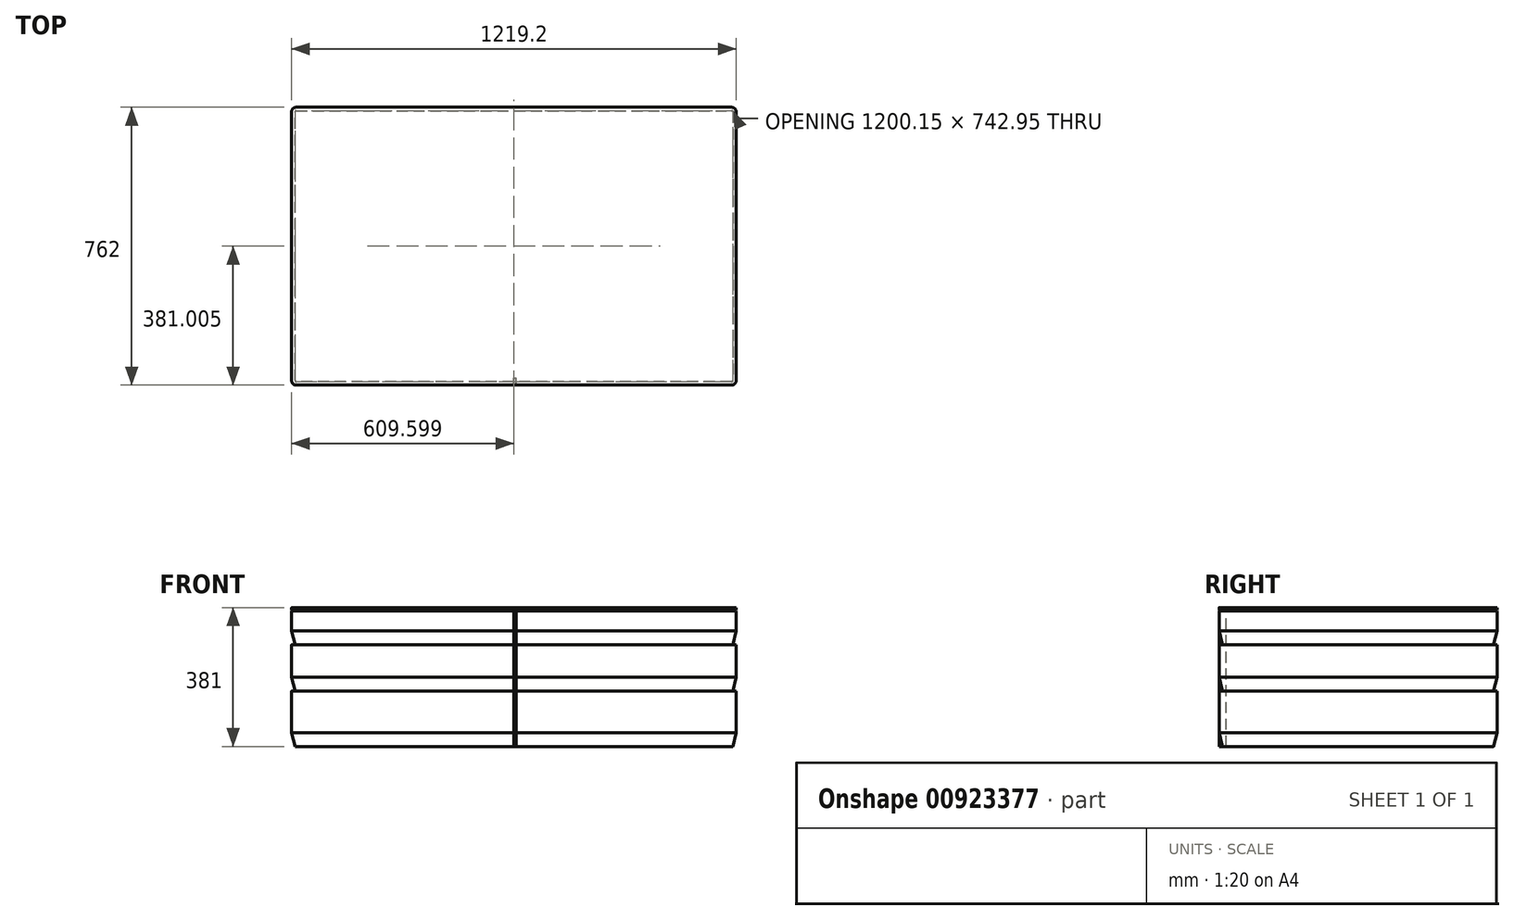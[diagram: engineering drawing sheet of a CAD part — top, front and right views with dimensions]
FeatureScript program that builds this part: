
annotation { "Feature Type Name" : "Feature", "Feature Type Description" : "" }
export const myFeature = defineFeature(function(context is Context, id is Id, definition is map)
    precondition{}
    {
        {
            var Q0;
            Q0=qCreatedBy(makeId("Top.planeOp"),FACE);
            var sketch = newSketch(context, id + "F0", { "sketchPlane" : qUnion([Q0])});
            skLineSegment(sketch, "E0.bottom", {"start": v(-1153.85, 736.91) * mm, "end": v(39.95, 736.91) * mm});
            skLineSegment(sketch, "E0.top", {"start": v(-1153.85, -25.09) * mm, "end": v(39.95, -25.09) * mm});
            skLineSegment(sketch, "E0.left", {"start": v(-1166.55, 724.21) * mm, "end": v(-1166.55, -12.39) * mm});
            skLineSegment(sketch, "E0.right", {"start": v(52.65, 724.21) * mm, "end": v(52.65, -12.39) * mm});
            skPoint(sketch, "E1.visualSharp", {"position": v(-1166.55, 736.91) * mm});
            skArc(sketch, "E1.filletArc", {"start": v(-1153.85, 736.91) * mm, "mid": v(-1162.83, 733.2) * mm, "end": v(-1166.55, 724.21) * mm});
            skPoint(sketch, "E2.visualSharp", {"position": v(-1166.55, -25.09) * mm});
            skArc(sketch, "E2.filletArc", {"start": v(-1166.55, -12.39) * mm, "mid": v(-1162.83, -21.37) * mm, "end": v(-1153.85, -25.09) * mm});
            skPoint(sketch, "E3.visualSharp", {"position": v(52.65, -25.09) * mm});
            skArc(sketch, "E3.filletArc", {"start": v(39.95, -25.09) * mm, "mid": v(48.93, -21.37) * mm, "end": v(52.65, -12.39) * mm});
            skPoint(sketch, "E4.visualSharp", {"position": v(52.65, 736.91) * mm});
            skArc(sketch, "E4.filletArc", {"start": v(52.65, 724.21) * mm, "mid": v(48.93, 733.2) * mm, "end": v(39.95, 736.91) * mm});
            skPoint(sketch, "E5", {"position": v(-556.95, -25.09) * mm});
            skLineSegment(sketch, "E6.bottom", {"start": v(-560.13, -25.09) * mm, "end": v(-553.78, -25.09) * mm});
            skLineSegment(sketch, "E7.left", {"start": v(-560.13, -25.09) * mm, "end": v(-560.13, -25.09) * mm});
            skLineSegment(sketch, "E7.right", {"start": v(-553.78, -25.09) * mm, "end": v(-553.78, -25.09) * mm});
            skLineSegment(sketch, "E8.top", {"start": v(-1166.55, 38.41) * mm, "end": v(-1103.05, 38.41) * mm});
            skLineSegment(sketch, "E8.right", {"start": v(-1103.05, -25.09) * mm, "end": v(-1103.05, 38.41) * mm});
            skLineSegment(sketch, "E9.bottom", {"start": v(-1166.55, 38.41) * mm, "end": v(-1147.5, 38.41) * mm});
            skLineSegment(sketch, "E9.left", {"start": v(-1166.55, 38.41) * mm, "end": v(-1166.55, 40) * mm});
            skLineSegment(sketch, "E10.bottom", {"start": v(-1103.05, -25.09) * mm, "end": v(-1101.46, -25.09) * mm});
            skLineSegment(sketch, "E10.left", {"start": v(-1103.05, -25.09) * mm, "end": v(-1103.05, -6.04) * mm});
            skSolve(sketch);
        }
        {
            var Q0;
            Q0=makeQuery(id+"F0.imprint","IMPRINT",FACE,{"disambiguationData":[TD([[makeQuery(id+"F0.imprint","IMPRINT",EDGE,{"derivedFrom":sQuery(id+"F0.wireOp",EDGE,"E0.bottom")}),-1.0]])]});
            var Q1;
            Q1=makeQuery(id+"F0.imprint","IMPRINT",FACE,{"disambiguationData":[TD([[makeQuery(id+"F0.imprint","IMPRINT",EDGE,{"derivedFrom":sQuery(id+"F0.wireOp",EDGE,"02rgMuwA-EyWu-0coL-EE2w-9yArAnqPD3th.bottom")}),-1.0]])]});
            var Q2;
            {var subQ0=sQuery(id+"F0.wireOp",EDGE,"JKqXYhlD-zWEc-dG3e-kvRR-2U4jhGjXMaC9.left");Q2=makeQuery(id+"F0.imprint","IMPRINT",FACE,{"disambiguationData":[TD([[makeQuery(id+"F0.imprint","IMPRINT",EDGE,{"derivedFrom":subQ0}),1.0]])]});}
            var Q3;
            {var subQ0=sQuery(id+"F0.wireOp",EDGE,"JKqXYhlD-zWEc-dG3e-kvRR-2U4jhGjXMaC9.bottom");Q3=makeQuery(id+"F0.imprint","IMPRINT",FACE,{"disambiguationData":[TD([[makeQuery(id+"F0.imprint","IMPRINT",EDGE,{"derivedFrom":subQ0}),1.0]])]});}
            var Q4;
            {var subQ0=sQuery(id+"F0.wireOp",EDGE,"JKqXYhlD-zWEc-dG3e-kvRR-2U4jhGjXMaC9.top");Q4=makeQuery(id+"F0.imprint","IMPRINT",FACE,{"disambiguationData":[TD([[makeQuery(id+"F0.imprint","IMPRINT",EDGE,{"derivedFrom":subQ0}),-1.0]])]});}
            var Q5;
            {var subQ0=sQuery(id+"F0.wireOp",EDGE,"JKqXYhlD-zWEc-dG3e-kvRR-2U4jhGjXMaC9.bottom");Q5=makeQuery(id+"F0.imprint","IMPRINT",FACE,{"disambiguationData":[TD([[makeQuery(id+"F0.imprint","IMPRINT",EDGE,{"derivedFrom":subQ0}),-1.0]])]});}
            var Q6;
            {var subQ0=sQuery(id+"F0.wireOp",EDGE,"JKqXYhlD-zWEc-dG3e-kvRR-2U4jhGjXMaC9.top");Q6=makeQuery(id+"F0.imprint","IMPRINT",FACE,{"disambiguationData":[TD([[makeQuery(id+"F0.imprint","IMPRINT",EDGE,{"derivedFrom":subQ0}),1.0]])]});}
            var Q7;
            {var subQ0=sQuery(id+"F0.wireOp",EDGE,"4L7YUCBR-3QsD-YcSa-PjCd-UrCzx3tGgLWM");Q7=makeQuery(id+"F0.imprint","IMPRINT",FACE,{"disambiguationData":[TD([[makeQuery(id+"F0.imprint","IMPRINT",EDGE,{"derivedFrom":subQ0}),1.0]])]});}
            var Q8;
            {var subQ0=sQuery(id+"F0.wireOp",EDGE,"B6Vmpnqa-0J3w-GW8c-4OqU-9oorpA2SGJfZ");Q8=makeQuery(id+"F0.imprint","IMPRINT",FACE,{"disambiguationData":[TD([[makeQuery(id+"F0.imprint","IMPRINT",EDGE,{"derivedFrom":subQ0}),-1.0]])]});}
            var Q9;
            Q9=makeQuery(id+"F0.imprint","IMPRINT",FACE,{"disambiguationData":[TD([[makeQuery(id+"F0.imprint","IMPRINT",EDGE,{"derivedFrom":sQuery(id+"F0.wireOp",EDGE,"E6.top")}),-1.0]])]});
            var Q10;
            {var subQ0=sQuery(id+"F0.wireOp",EDGE,"E2.filletArc");Q10=makeQuery(id+"F0.imprint","IMPRINT",FACE,{"disambiguationData":[TD([[makeQuery(id+"F0.imprint","IMPRINT",EDGE,{"derivedFrom":subQ0}),1.0]])]});}
            var Q11;
            Q11=makeQuery(id+"F0.imprint","IMPRINT",FACE,{"disambiguationData":[TD([[makeQuery(id+"F0.imprint","IMPRINT",EDGE,{"derivedFrom":sQuery(id+"F0.wireOp",EDGE,"E9.bottom")}),1.0]])]});
            var Q12;
            Q12=makeQuery(id+"F0.imprint","IMPRINT",FACE,{"disambiguationData":[TD([[makeQuery(id+"F0.imprint","IMPRINT",EDGE,{"derivedFrom":sQuery(id+"F0.wireOp",EDGE,"E10.bottom")}),1.0]])]});
            extrude(context, id + "F1", {"entities" : qUnion([Q0, Q1, Q2, Q3, Q4, Q5, Q6, Q7, Q8, Q9, Q10, Q11, Q12]), "oppositeDirection" : true, "depth" : 6.35 * mm, "offsetDistance" : 25.4 * mm});
        }
        {
            var Q0;
            Q0=makeQuery(id+"F0.imprint","IMPRINT",FACE,{"disambiguationData":[TD([[makeQuery(id+"F0.imprint","IMPRINT",EDGE,{"derivedFrom":sQuery(id+"F0.wireOp",EDGE,"E0.bottom")}),-1.0]])]});
            var Q1;
            Q1=makeQuery(id+"F0.imprint","IMPRINT",FACE,{"disambiguationData":[TD([[makeQuery(id+"F0.imprint","IMPRINT",EDGE,{"derivedFrom":sQuery(id+"F0.wireOp",EDGE,"02rgMuwA-EyWu-0coL-EE2w-9yArAnqPD3th.bottom")}),-1.0]])]});
            var Q2;
            Q2=makeQuery(id+"F0.imprint","IMPRINT",FACE,{"disambiguationData":[TD([[makeQuery(id+"F0.imprint","IMPRINT",EDGE,{"derivedFrom":sQuery(id+"F0.wireOp",EDGE,"JKqXYhlD-zWEc-dG3e-kvRR-2U4jhGjXMaC9.bottom")}),-1.0]])]});
            var Q3;
            {var subQ0=sQuery(id+"F0.wireOp",EDGE,"E2.filletArc");Q3=makeQuery(id+"F0.imprint","IMPRINT",FACE,{"disambiguationData":[TD([[makeQuery(id+"F0.imprint","IMPRINT",EDGE,{"derivedFrom":subQ0}),1.0]])]});}
            extrude(context, id + "F2", {"entities" : qUnion([Q0, Q1, Q2, Q3]), "oppositeDirection" : true, "depth" : 101.6 * mm, "offsetDistance" : 25.4 * mm, "hasSecondDirection" : true, "secondDirectionOppositeDirection" : true, "secondDirectionDepth" : 9.52 * mm});
        }
        {
            var Q0;
            Q0=makeQuery(id+"F2.opExtrude","CAP_FACE",FACE,{"disambiguationData":[OSD([sQuery(id+"F0.wireOp",EDGE,"E0.bottom"),sQuery(id+"F0.wireOp",EDGE,"E0.top"),sQuery(id+"F0.wireOp",EDGE,"E0.left"),sQuery(id+"F0.wireOp",EDGE,"E0.right"),sQuery(id+"F0.wireOp",EDGE,"E1.filletArc"),sQuery(id+"F0.wireOp",EDGE,"E2.filletArc"),sQuery(id+"F0.wireOp",EDGE,"E3.filletArc"),sQuery(id+"F0.wireOp",EDGE,"E4.filletArc")])],"isStart":false});
            chamfer(context, id + "F3", {"entities" : qUnion([Q0]), "chamferType" : ChamferType.TWO_OFFSETS, "width1" : 38.1 * mm, "oppositeDirection" : true, "width2" : 9.52 * mm, "tangentPropagation" : true});
        }
        {
            var Q0;
            Q0=makeQuery(id+"F0.imprint","IMPRINT",FACE,{"disambiguationData":[TD([[makeQuery(id+"F0.imprint","IMPRINT",EDGE,{"derivedFrom":sQuery(id+"F0.wireOp",EDGE,"E0.bottom")}),-1.0]])]});
            var Q1;
            Q1=makeQuery(id+"F0.imprint","IMPRINT",FACE,{"disambiguationData":[TD([[makeQuery(id+"F0.imprint","IMPRINT",EDGE,{"derivedFrom":sQuery(id+"F0.wireOp",EDGE,"JKqXYhlD-zWEc-dG3e-kvRR-2U4jhGjXMaC9.bottom")}),-1.0]])]});
            var Q2;
            Q2=makeQuery(id+"F0.imprint","IMPRINT",FACE,{"disambiguationData":[TD([[makeQuery(id+"F0.imprint","IMPRINT",EDGE,{"derivedFrom":sQuery(id+"F0.wireOp",EDGE,"02rgMuwA-EyWu-0coL-EE2w-9yArAnqPD3th.bottom")}),-1.0]])]});
            var Q3;
            {var subQ0=sQuery(id+"F0.wireOp",EDGE,"E2.filletArc");Q3=makeQuery(id+"F0.imprint","IMPRINT",FACE,{"disambiguationData":[TD([[makeQuery(id+"F0.imprint","IMPRINT",EDGE,{"derivedFrom":subQ0}),1.0]])]});}
            extrude(context, id + "F4", {"entities" : qUnion([Q0, Q1, Q2, Q3]), "operationType" : NewBodyOperationType.ADD, "oppositeDirection" : true, "depth" : 228.6 * mm, "offsetDistance" : 25.4 * mm, "hasSecondDirection" : true, "secondDirectionOppositeDirection" : true, "secondDirectionDepth" : 101.6 * mm});
        }
        {
            var Q0;
            Q0=makeQuery(id+"F4.opExtrude","CAP_FACE",FACE,{"disambiguationData":[OSD([sQuery(id+"F0.wireOp",EDGE,"E0.bottom"),sQuery(id+"F0.wireOp",EDGE,"E0.top"),sQuery(id+"F0.wireOp",EDGE,"E0.left"),sQuery(id+"F0.wireOp",EDGE,"E0.right")])],"isStart":false});
            chamfer(context, id + "F5", {"entities" : qUnion([Q0]), "chamferType" : ChamferType.TWO_OFFSETS, "width1" : 38.1 * mm, "oppositeDirection" : true, "width2" : 9.52 * mm, "tangentPropagation" : true});
        }
        {
            var Q0;
            Q0=makeQuery(id+"F0.imprint","IMPRINT",FACE,{"disambiguationData":[TD([[makeQuery(id+"F0.imprint","IMPRINT",EDGE,{"derivedFrom":sQuery(id+"F0.wireOp",EDGE,"E0.bottom")}),-1.0]])]});
            var Q1;
            Q1=makeQuery(id+"F0.imprint","IMPRINT",FACE,{"disambiguationData":[TD([[makeQuery(id+"F0.imprint","IMPRINT",EDGE,{"derivedFrom":sQuery(id+"F0.wireOp",EDGE,"JKqXYhlD-zWEc-dG3e-kvRR-2U4jhGjXMaC9.bottom")}),-1.0]])]});
            var Q2;
            Q2=makeQuery(id+"F0.imprint","IMPRINT",FACE,{"disambiguationData":[TD([[makeQuery(id+"F0.imprint","IMPRINT",EDGE,{"derivedFrom":sQuery(id+"F0.wireOp",EDGE,"02rgMuwA-EyWu-0coL-EE2w-9yArAnqPD3th.bottom")}),-1.0]])]});
            var Q3;
            {var subQ0=sQuery(id+"F0.wireOp",EDGE,"E2.filletArc");Q3=makeQuery(id+"F0.imprint","IMPRINT",FACE,{"disambiguationData":[TD([[makeQuery(id+"F0.imprint","IMPRINT",EDGE,{"derivedFrom":subQ0}),1.0]])]});}
            extrude(context, id + "F6", {"entities" : qUnion([Q0, Q1, Q2, Q3]), "operationType" : NewBodyOperationType.ADD, "oppositeDirection" : true, "depth" : 381 * mm, "offsetDistance" : 25.4 * mm, "hasSecondDirection" : true, "secondDirectionOppositeDirection" : true, "secondDirectionDepth" : 228.6 * mm});
        }
        {
            var Q0;
            Q0=makeQuery(id+"F6.opExtrude","CAP_FACE",FACE,{"disambiguationData":[OSD([sQuery(id+"F0.wireOp",EDGE,"E0.bottom"),sQuery(id+"F0.wireOp",EDGE,"E0.top"),sQuery(id+"F0.wireOp",EDGE,"E0.left"),sQuery(id+"F0.wireOp",EDGE,"E0.right")])],"isStart":false});
            chamfer(context, id + "F7", {"entities" : qUnion([Q0]), "chamferType" : ChamferType.TWO_OFFSETS, "width1" : 38.1 * mm, "oppositeDirection" : true, "width2" : 9.52 * mm, "tangentPropagation" : true});
        }
        {
            var Q0;
            Q0=makeQuery(id+"F1.opExtrude","CAP_FACE",FACE,{"disambiguationData":[OSD([sQuery(id+"F0.wireOp",EDGE,"E0.bottom"),sQuery(id+"F0.wireOp",EDGE,"E0.top"),sQuery(id+"F0.wireOp",EDGE,"E0.left"),sQuery(id+"F0.wireOp",EDGE,"E0.right"),sQuery(id+"F0.wireOp",EDGE,"E1.filletArc"),sQuery(id+"F0.wireOp",EDGE,"E2.filletArc"),sQuery(id+"F0.wireOp",EDGE,"E3.filletArc"),sQuery(id+"F0.wireOp",EDGE,"E4.filletArc"),sQuery(id+"F0.wireOp",EDGE,"E6.bottom"),sQuery(id+"F0.wireOp",EDGE,"E9.left"),sQuery(id+"F0.wireOp",EDGE,"E10.bottom")])],"isStart":true});
            var sketch = newSketch(context, id + "F8", { "sketchPlane" : qUnion([Q0])});
            skLineSegment(sketch, "E11.bottom", {"start": v(-556.95, -25.09) * mm, "end": v(-550.6, -25.09) * mm});
            skLineSegment(sketch, "E11.top", {"start": v(-556.95, -6.04) * mm, "end": v(-550.6, -6.04) * mm});
            skLineSegment(sketch, "E11.left", {"start": v(-556.95, -25.09) * mm, "end": v(-556.95, -6.04) * mm});
            skLineSegment(sketch, "E11.right", {"start": v(-550.6, -25.09) * mm, "end": v(-550.6, -6.04) * mm});
            skLineSegment(sketch, "E12.left", {"start": v(-556.95, -25.09) * mm, "end": v(-556.95, -25.09) * mm});
            skLineSegment(sketch, "E12.right", {"start": v(-550.6, -25.09) * mm, "end": v(-550.6, -25.09) * mm});
            skLineSegment(sketch, "E13.top", {"start": v(-556.95, -28.26) * mm, "end": v(-550.6, -28.26) * mm});
            skLineSegment(sketch, "E13.left", {"start": v(-556.95, -25.09) * mm, "end": v(-556.95, -28.26) * mm});
            skLineSegment(sketch, "E13.right", {"start": v(-550.6, -25.09) * mm, "end": v(-550.6, -28.26) * mm});
            skSolve(sketch);
        }
        {
            var Q0;
            Q0=makeQuery(id+"F8.imprint","IMPRINT",FACE,{"disambiguationData":[TD([[makeQuery(id+"F8.imprint","IMPRINT",EDGE,{"derivedFrom":sQuery(id+"F8.wireOp",EDGE,"E11.bottom")}),-1.0]])]});
            var Q1;
            Q1=makeQuery(id+"F8.imprint","IMPRINT",FACE,{"disambiguationData":[TD([[makeQuery(id+"F8.imprint","IMPRINT",EDGE,{"derivedFrom":sQuery(id+"F8.wireOp",EDGE,"E11.top")}),-1.0]])]});
            extrude(context, id + "F9", {"entities" : qUnion([Q0, Q1]), "oppositeDirection" : true, "depth" : 381 * mm, "offsetDistance" : 25.4 * mm, "hasSecondDirection" : true, "secondDirectionOppositeDirection" : true, "secondDirectionDepth" : 9.52 * mm});
        }
    });
